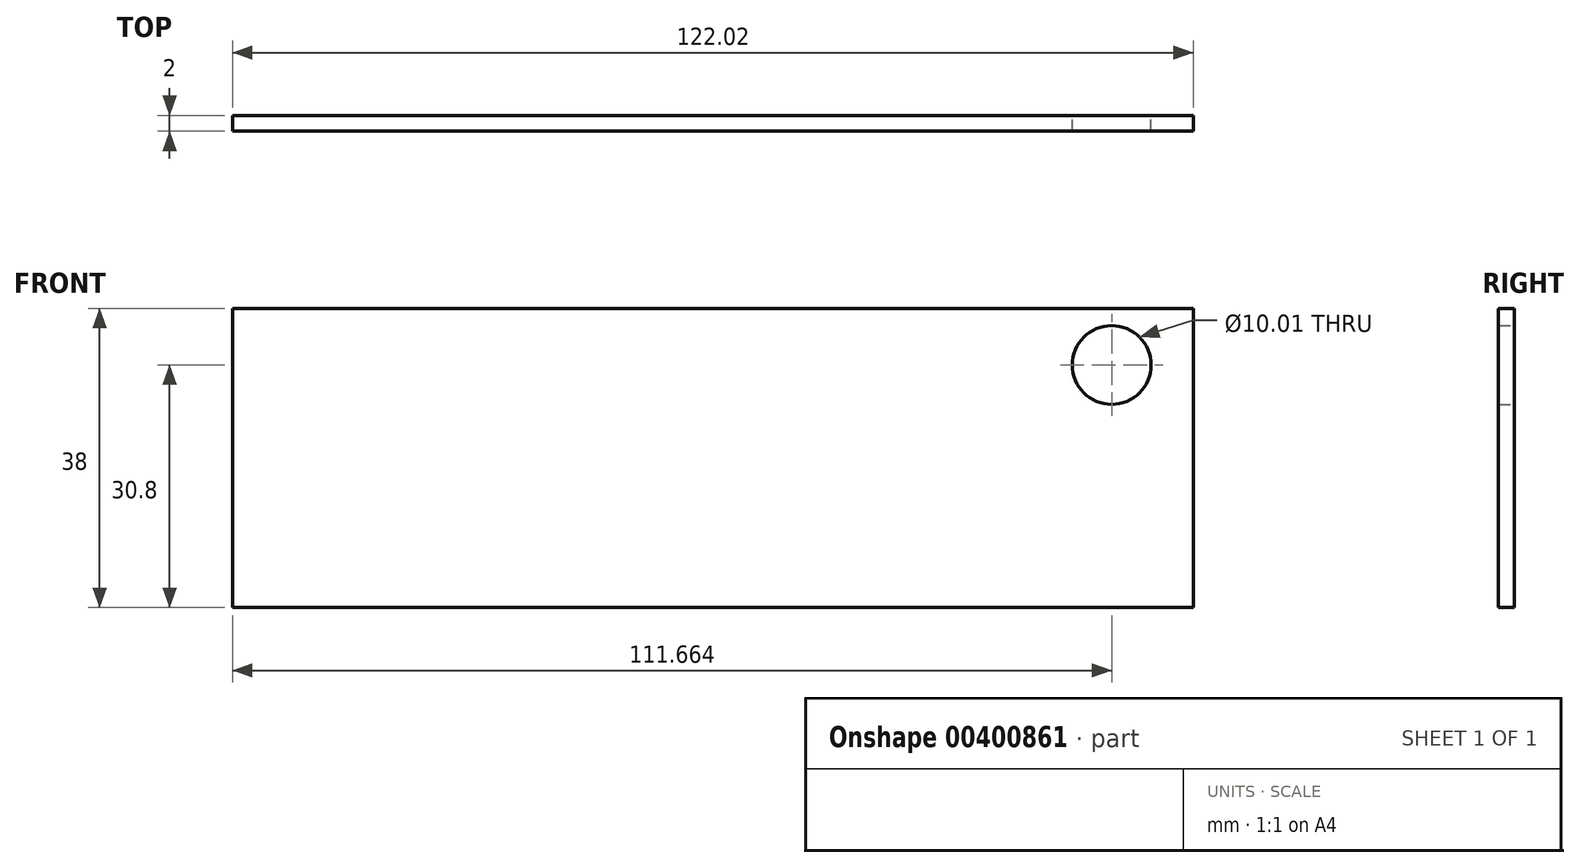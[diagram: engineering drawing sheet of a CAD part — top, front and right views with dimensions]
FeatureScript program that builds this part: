
annotation { "Feature Type Name" : "Feature", "Feature Type Description" : "" }
export const myFeature = defineFeature(function(context is Context, id is Id, definition is map)
    precondition{}
    {
        {
            var Q0;
            Q0=qCreatedBy(makeId("Front.planeOp"),FACE);
            var sketch = newSketch(context, id + "F0", { "sketchPlane" : qUnion([Q0])});
            skLineSegment(sketch, "E0.bottom", {"start": v(61.01, -19) * mm, "end": v(-61.01, -19) * mm});
            skLineSegment(sketch, "E0.top", {"start": v(61.01, 19) * mm, "end": v(-61.01, 19) * mm});
            skLineSegment(sketch, "E0.left", {"start": v(61.01, -19) * mm, "end": v(61.01, 19) * mm});
            skLineSegment(sketch, "E0.right", {"start": v(-61.01, -19) * mm, "end": v(-61.01, 19) * mm});
            skPoint(sketch, "E0.middle", {"position": v(0, 0) * mm});
            skSolve(sketch);
        }
        {
            var Q0;
            Q0=qCreatedBy(makeId("Front.planeOp"),FACE);
            var sketch = newSketch(context, id + "F1", { "sketchPlane" : qUnion([Q0])});
            skText(sketch, "E1", { "text": "Yooper", "fontName": "OpenSans-Bold.ttf"});
            const initialGuessF1  = {"E1": [-0.05238, -0.01065, 1, 0, 0.02015]};
            skSetInitialGuess(sketch, initialGuessF1);
            skSolve(sketch);
        }
        {
            var Q0;
            Q0 = qSketchRegion(id + "F1", true);
            var Q1;
            Q1 = qConstructionFilter(qBodyType(qCreatedBy(id + "F1" ,EDGE), BodyType.WIRE), ConstructionObject.NO);
            extrude(context, id + "F2", {"entities" : qUnion([Q0]), "bodyType" : ToolBodyType.SURFACE, "surfaceEntities" : qUnion([Q1]), "depth" : 5 * mm});
        }
        {
            var Q0;
            Q0=makeQuery(id+"F0.imprint","IMPRINT",FACE,{"disambiguationData":[TD([[makeQuery(id+"F0.imprint","IMPRINT",EDGE,{"derivedFrom":sQuery(id+"F0.wireOp",EDGE,"E0.bottom")}),-1.0]])]});
            extrude(context, id + "F3", {"entities" : qUnion([Q0]), "depth" : 2 * mm});
        }
        {
            var Q0;
            Q0=qCreatedBy(makeId("Front.planeOp"),FACE);
            var sketch = newSketch(context, id + "F4", { "sketchPlane" : qUnion([Q0])});
            skPoint(sketch, "E2", {"position": v(50.65, 11.8) * mm});
            skSolve(sketch);
        }
        {
            var Q0;
            Q0=sQuery(id+"F4.wireOp",VERTEX,"E2");
            var Q1;
            Q1=makeQuery(id+"F3.opExtrude","SWEPT_BODY",BODY,{"disambiguationData":[OSD([sQuery(id+"F0.wireOp",EDGE,"E0.bottom"),sQuery(id+"F0.wireOp",EDGE,"E0.top"),sQuery(id+"F0.wireOp",EDGE,"E0.left"),sQuery(id+"F0.wireOp",EDGE,"E0.right")])]});
            hole(context, id + "F5", {"style" : HoleStyle.C_BORE, "endStyle" : HoleEndStyle.THROUGH, "oppositeDirection" : true, "holeDiameter" : 10 * mm, "cBoreDiameter" : 10 * mm, "cBoreDepth" : 5 * mm, "isTappedThrough" : true, "tappedDepth" : 12.7 * mm, "tapClearance" : 3, "startFromSketch" : true, "locations" : qUnion([Q0]), "scope" : qUnion([Q1])});
        }
    });
